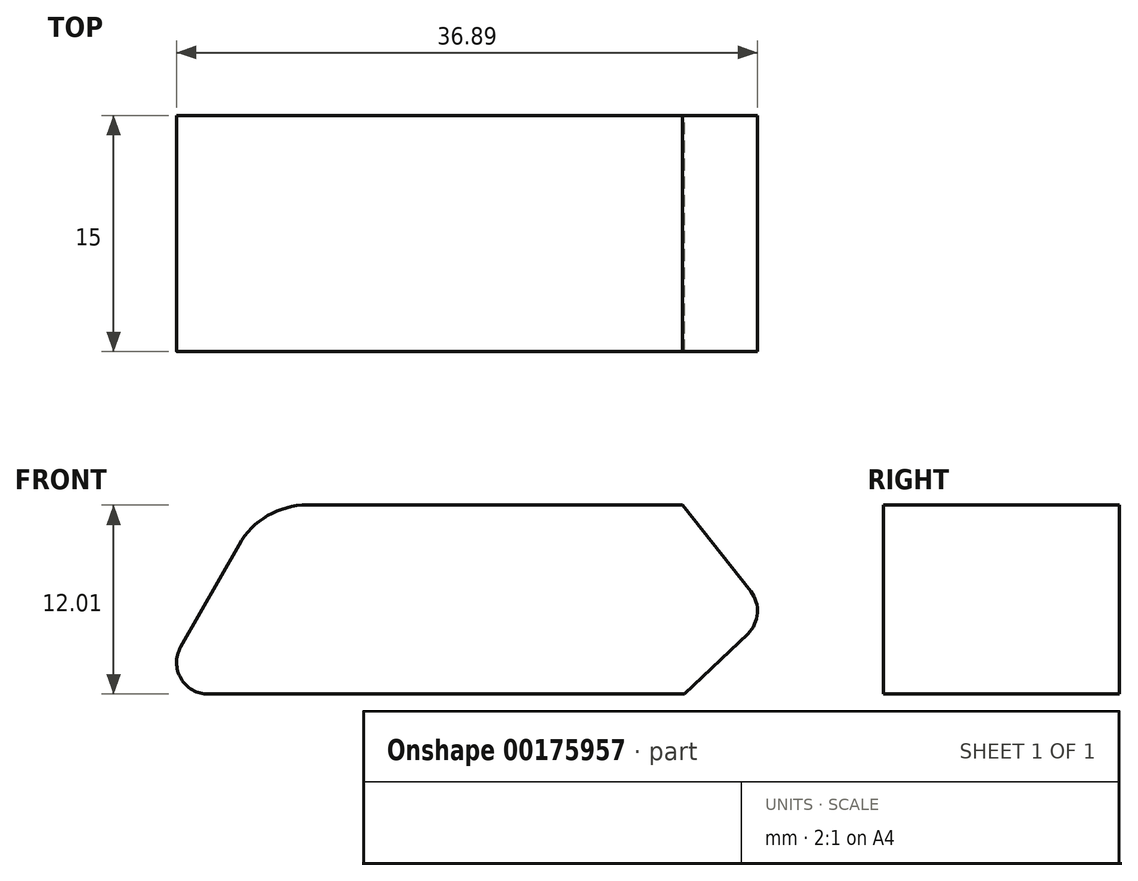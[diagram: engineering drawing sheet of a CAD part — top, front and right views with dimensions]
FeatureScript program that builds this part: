
annotation { "Feature Type Name" : "Feature", "Feature Type Description" : "" }
export const myFeature = defineFeature(function(context is Context, id is Id, definition is map)
    precondition{}
    {
        {
            var Q0;
            Q0=qCreatedBy(makeId("Front.planeOp"),FACE);
            var sketch = newSketch(context, id + "F0", { "sketchPlane" : qUnion([Q0])});
            skLineSegment(sketch, "E0", {"start": v(-30.25, 0) * mm, "end": v(0, 0) * mm});
            skLineSegment(sketch, "E1", {"start": v(0, 0) * mm, "end": v(4.02, 3.84) * mm});
            skLineSegment(sketch, "E2", {"start": v(4.21, 6.52) * mm, "end": v(-0.13, 12.01) * mm});
            skLineSegment(sketch, "E3", {"start": v(-0.13, 12.01) * mm, "end": v(-13.88, 12.01) * mm});
            skLineSegment(sketch, "E4", {"start": v(-13.88, 12.01) * mm, "end": v(-23.95, 12.01) * mm});
            skLineSegment(sketch, "E5", {"start": v(-28.3, 9.48) * mm, "end": v(-32, 2.99) * mm});
            skPoint(sketch, "E6.visualSharp", {"position": v(5.34, 5.1) * mm});
            skArc(sketch, "E6.filletArc", {"start": v(4.02, 3.84) * mm, "mid": v(4.64, 5.14) * mm, "end": v(4.21, 6.52) * mm});
            skPoint(sketch, "E7.visualSharp", {"position": v(-26.86, 12.01) * mm});
            skArc(sketch, "E7.filletArc", {"start": v(-23.95, 12.01) * mm, "mid": v(-26.47, 11.33) * mm, "end": v(-28.3, 9.48) * mm});
            skPoint(sketch, "E8.visualSharp", {"position": v(-33.69, 0) * mm});
            skArc(sketch, "E8.filletArc", {"start": v(-32, 2.99) * mm, "mid": v(-31.98, 1) * mm, "end": v(-30.25, 0) * mm});
            skSolve(sketch);
        }
        {
            var Q0;
            Q0 = qSketchRegion(id + "F0", true);
            extrude(context, id + "F1", {"entities" : qUnion([Q0]), "depth" : 15 * mm});
        }
    });
